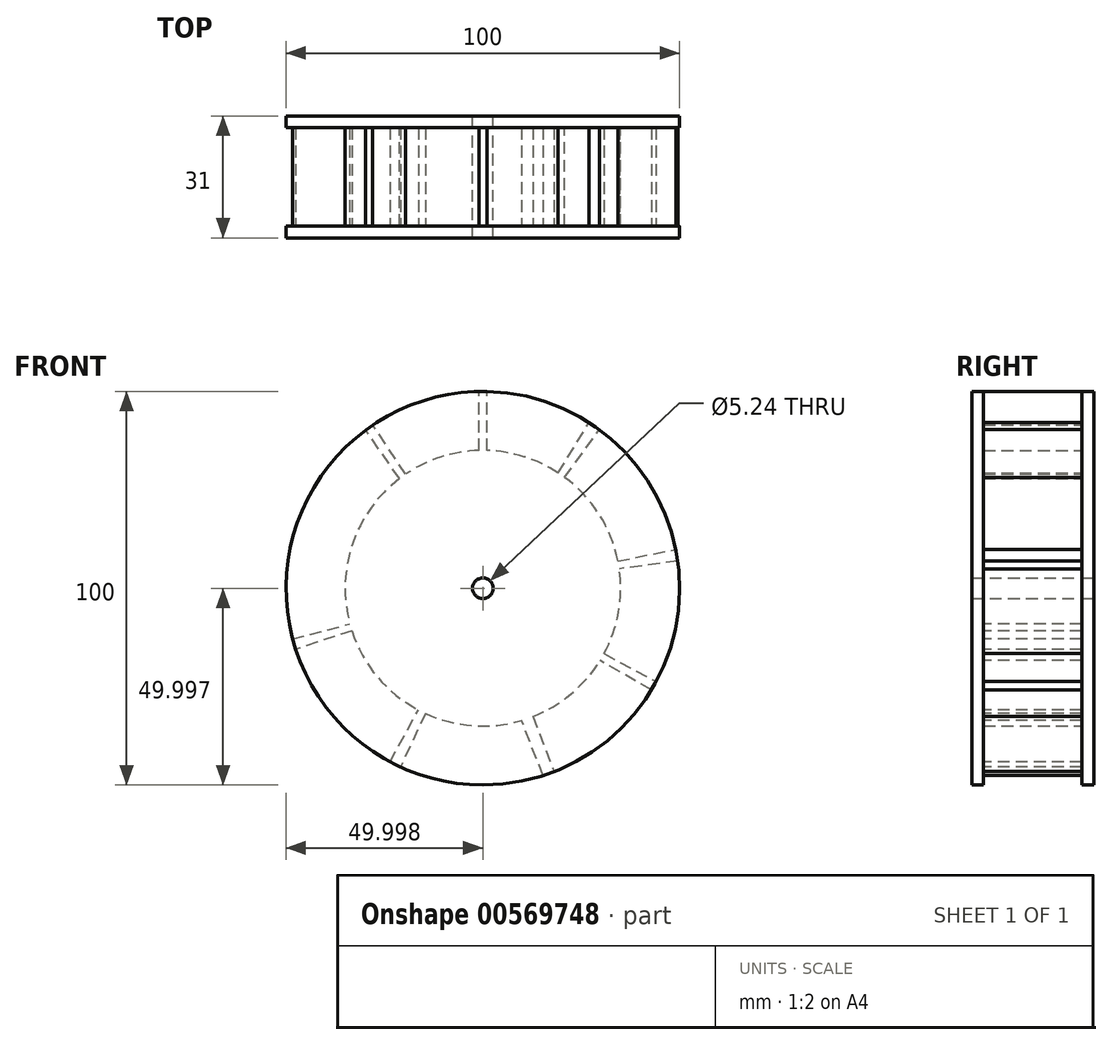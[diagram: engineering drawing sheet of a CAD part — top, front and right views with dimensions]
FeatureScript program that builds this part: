
annotation { "Feature Type Name" : "Feature", "Feature Type Description" : "" }
export const myFeature = defineFeature(function(context is Context, id is Id, definition is map)
    precondition{}
    {
        {
            var Q0;
            Q0=qCreatedBy(makeId("Front.planeOp"),FACE);
            var sketch = newSketch(context, id + "F0", { "sketchPlane" : qUnion([Q0])});
            skCircle(sketch, "E0", {"center": v(-6.77, 6) * mm, "radius": 50 * mm});
            skSolve(sketch);
        }
        {
            var Q0;
            Q0=makeQuery(id+"F0.imprint","IMPRINT",FACE,{"disambiguationData":[TD([[makeQuery(id+"F0.imprint","IMPRINT",EDGE,{"derivedFrom":sQuery(id+"F0.wireOp",EDGE,"E0")}),1.0]])]});
            extrude(context, id + "F1", {"entities" : qUnion([Q0]), "depth" : 3 * mm, "offsetDistance" : 25 * mm});
        }
        {
            var Q0;
            Q0=makeQuery(id+"F1.opExtrude","CAP_FACE",FACE,{"disambiguationData":[OSD([sQuery(id+"F0.wireOp",EDGE,"E0")])],"isStart":false});
            var sketch = newSketch(context, id + "F2", { "sketchPlane" : qUnion([Q0])});
            skCircle(sketch, "E1", {"center": v(-6.77, 6) * mm, "radius": 35 * mm});
            skSolve(sketch);
        }
        {
            var Q0;
            Q0=makeQuery(id+"F2.imprint","IMPRINT",FACE,{"disambiguationData":[TD([[makeQuery(id+"F2.imprint","IMPRINT",EDGE,{"derivedFrom":sQuery(id+"F2.wireOp",EDGE,"E1")}),1.0]])]});
            extrude(context, id + "F3", {"entities" : qUnion([Q0]), "operationType" : NewBodyOperationType.ADD, "depth" : 25 * mm, "offsetDistance" : 25 * mm});
        }
        {
            var Q0;
            Q0=makeQuery(id+"F3.opExtrude","CAP_FACE",FACE,{"disambiguationData":[OSD([sQuery(id+"F2.wireOp",EDGE,"E1")])],"isStart":false});
            var sketch = newSketch(context, id + "F4", { "sketchPlane" : qUnion([Q0])});
            skCircle(sketch, "E2", {"center": v(-6.77, 6) * mm, "radius": 50 * mm});
            skSolve(sketch);
        }
        {
            var Q0;
            Q0=makeQuery(id+"F4.imprint","IMPRINT",FACE,{"disambiguationData":[TD([[makeQuery(id+"F4.imprint","IMPRINT",EDGE,{"derivedFrom":makeQuery(id+"F3.opExtrude","CAP_EDGE",EDGE,{"disambiguationData":[OSD([sQuery(id+"F2.wireOp",EDGE,"E1")])],"isStart":false})}),1.0]])]});
            var Q1;
            Q1=makeQuery(id+"F4.imprint","IMPRINT",FACE,{"disambiguationData":[TD([[makeQuery(id+"F4.imprint","IMPRINT",EDGE,{"derivedFrom":sQuery(id+"F4.wireOp",EDGE,"E2")}),1.0]])]});
            extrude(context, id + "F5", {"entities" : qUnion([Q0, Q1]), "operationType" : NewBodyOperationType.ADD, "depth" : 3 * mm, "offsetDistance" : 25 * mm});
        }
        {
            var Q0;
            Q0=makeQuery(id+"F1.opExtrude","CAP_FACE",FACE,{"disambiguationData":[OSD([sQuery(id+"F0.wireOp",EDGE,"E0")])],"isStart":false});
            var sketch = newSketch(context, id + "F6", { "sketchPlane" : qUnion([Q0])});
            skLineSegment(sketch, "E3.bottom", {"start": v(-7.68, 41) * mm, "end": v(-5.68, 41) * mm});
            skLineSegment(sketch, "E3.top", {"start": v(-7.68, 56) * mm, "end": v(-5.68, 56) * mm});
            skLineSegment(sketch, "E3.left", {"start": v(-7.68, 41) * mm, "end": v(-7.68, 56) * mm});
            skLineSegment(sketch, "E3.right", {"start": v(-5.68, 41) * mm, "end": v(-5.68, 56) * mm});
            skLineSegment(sketch, "E4", {"start": v(-26.36, 35.01) * mm, "end": v(-34.75, 47.44) * mm});
            skLineSegment(sketch, "E5", {"start": v(-34.75, 47.44) * mm, "end": v(-36.53, 46.19) * mm});
            skLineSegment(sketch, "E6", {"start": v(-36.53, 46.19) * mm, "end": v(-27.98, 33.85) * mm});
            skLineSegment(sketch, "E7", {"start": v(-27.98, 33.85) * mm, "end": v(-26.36, 35.01) * mm});
            skLineSegment(sketch, "E8", {"start": v(12.34, 35.33) * mm, "end": v(20.24, 48.09) * mm});
            skLineSegment(sketch, "E9", {"start": v(20.24, 48.09) * mm, "end": v(22.87, 46.27) * mm});
            skLineSegment(sketch, "E10", {"start": v(22.87, 46.27) * mm, "end": v(13.98, 34.2) * mm});
            skLineSegment(sketch, "E11", {"start": v(12.34, 35.33) * mm, "end": v(13.98, 34.2) * mm});
            skSolve(sketch);
        }
        {
            var Q0;
            {var subQ0=sQuery(id+"F6.wireOp",EDGE,"E4");Q0=makeQuery(id+"F6.imprint","IMPRINT",FACE,{"disambiguationData":[TD([[makeQuery(id+"F6.imprint","IMPRINT",EDGE,{"derivedFrom":subQ0}),1.0]])]});}
            var Q1;
            Q1=makeQuery(id+"F6.imprint","IMPRINT",FACE,{"disambiguationData":[TD([[makeQuery(id+"F6.imprint","IMPRINT",EDGE,{"derivedFrom":sQuery(id+"F6.wireOp",EDGE,"E3.top")}),-1.0]])]});
            var Q2;
            {var subQ0=sQuery(id+"F6.wireOp",EDGE,"E8");Q2=makeQuery(id+"F6.imprint","IMPRINT",FACE,{"disambiguationData":[TD([[makeQuery(id+"F6.imprint","IMPRINT",EDGE,{"derivedFrom":subQ0}),-1.0]])]});}
            extrude(context, id + "F7", {"entities" : qUnion([Q0, Q1, Q2]), "operationType" : NewBodyOperationType.ADD, "depth" : 28 * mm, "offsetDistance" : 25 * mm});
        }
        {
            var Q0;
            {var subQ0=sQuery(id+"F4.wireOp",EDGE,"E2");var subQ1=makeQuery(id+"F5.opExtrude","CAP_FACE",FACE,{"disambiguationData":[OSD([subQ0])],"isStart":true});Q0=makeQuery(id+"F7.boolean.opBoolean","SPLIT",FACE,{"disambiguationData":[TD([makeQuery(id+"F3.opExtrude","SWEPT_FACE",FACE,{"disambiguationData":[OSD([sQuery(id+"F2.wireOp",EDGE,"E1")])]}),makeQuery(id+"F5.opExtrude","SWEPT_FACE",FACE,{"disambiguationData":[OSD([subQ0])]}),subQ1,makeQuery(id+"F7.opExtrude","SWEPT_FACE",FACE,{"disambiguationData":[OSD([sQuery(id+"F6.wireOp",EDGE,"E5")])]}),makeQuery(id+"F7.opExtrude","SWEPT_FACE",FACE,{"disambiguationData":[OSD([sQuery(id+"F6.wireOp",EDGE,"E6")])]}),makeQuery(id+"F7.opExtrude","SWEPT_FACE",FACE,{"disambiguationData":[OSD([sQuery(id+"F6.wireOp",EDGE,"E9")])]}),makeQuery(id+"F7.opExtrude","SWEPT_FACE",FACE,{"disambiguationData":[OSD([sQuery(id+"F6.wireOp",EDGE,"E10")])]})])],"derivedFrom":subQ1});}
            var sketch = newSketch(context, id + "F8", { "sketchPlane" : qUnion([Q0])});
            skLineSegment(sketch, "E12", {"start": v(-27.54, 12.9) * mm, "end": v(-42.25, 15.87) * mm});
            skLineSegment(sketch, "E13", {"start": v(-42.25, 15.87) * mm, "end": v(-42.75, 12.9) * mm});
            skLineSegment(sketch, "E14", {"start": v(-42.75, 12.9) * mm, "end": v(-27.88, 10.94) * mm});
            skLineSegment(sketch, "E15", {"start": v(-27.88, 10.94) * mm, "end": v(-27.54, 12.9) * mm});
            skLineSegment(sketch, "E16", {"start": v(-24.03, -10.6) * mm, "end": v(-37.24, -17.72) * mm});
            skLineSegment(sketch, "E17", {"start": v(-37.24, -17.72) * mm, "end": v(-36.05, -19.8) * mm});
            skLineSegment(sketch, "E18", {"start": v(-36.05, -19.8) * mm, "end": v(-23.01, -12.37) * mm});
            skLineSegment(sketch, "E19", {"start": v(-23.01, -12.37) * mm, "end": v(-24.03, -10.6) * mm});
            skLineSegment(sketch, "E20", {"start": v(-5.92, -26.61) * mm, "end": v(-11.36, -40.6) * mm});
            skLineSegment(sketch, "E21", {"start": v(-11.36, -40.6) * mm, "end": v(-8.53, -41.6) * mm});
            skLineSegment(sketch, "E22", {"start": v(-8.53, -41.6) * mm, "end": v(-3.08, -27.58) * mm});
            skLineSegment(sketch, "E23", {"start": v(-3.08, -27.58) * mm, "end": v(-5.92, -26.61) * mm});
            skSolve(sketch);
        }
        {
            var Q0;
            {var subQ0=sQuery(id+"F8.wireOp",EDGE,"E12");Q0=makeQuery(id+"F8.imprint","IMPRINT",FACE,{"disambiguationData":[TD([[makeQuery(id+"F8.imprint","IMPRINT",EDGE,{"derivedFrom":subQ0}),1.0]])]});}
            var Q1;
            {var subQ0=sQuery(id+"F8.wireOp",EDGE,"E16");Q1=makeQuery(id+"F8.imprint","IMPRINT",FACE,{"disambiguationData":[TD([[makeQuery(id+"F8.imprint","IMPRINT",EDGE,{"derivedFrom":subQ0}),1.0]])]});}
            var Q2;
            {var subQ0=sQuery(id+"F8.wireOp",EDGE,"E20");Q2=makeQuery(id+"F8.imprint","IMPRINT",FACE,{"disambiguationData":[TD([[makeQuery(id+"F8.imprint","IMPRINT",EDGE,{"derivedFrom":subQ0}),1.0]])]});}
            extrude(context, id + "F9", {"entities" : qUnion([Q0, Q1, Q2]), "operationType" : NewBodyOperationType.ADD, "depth" : 28 * mm, "offsetDistance" : 25 * mm});
        }
        {
            var Q0;
            {var subQ0=makeQuery(id+"F7.opExtrude","SWEPT_FACE",FACE,{"disambiguationData":[OSD([sQuery(id+"F6.wireOp",EDGE,"E5")])]});var subQ1=sQuery(id+"F4.wireOp",EDGE,"E2");var subQ2=makeQuery(id+"F5.opExtrude","SWEPT_FACE",FACE,{"disambiguationData":[OSD([subQ1])]});var subQ3=makeQuery(id+"F5.opExtrude","CAP_FACE",FACE,{"disambiguationData":[OSD([subQ1])],"isStart":true});var subQ4=makeQuery(id+"F3.opExtrude","SWEPT_FACE",FACE,{"disambiguationData":[OSD([sQuery(id+"F2.wireOp",EDGE,"E1")])]});var subQ5=makeQuery(id+"F7.opExtrude","SWEPT_FACE",FACE,{"disambiguationData":[OSD([sQuery(id+"F6.wireOp",EDGE,"E6")])]});Q0=makeQuery(id+"F9.boolean.opBoolean","SPLIT",FACE,{"disambiguationData":[TD([subQ4,subQ2,subQ3,subQ0,subQ5,makeQuery(id+"F9.opExtrude","SWEPT_FACE",FACE,{"disambiguationData":[OSD([sQuery(id+"F8.wireOp",EDGE,"E21")])]}),makeQuery(id+"F9.opExtrude","SWEPT_FACE",FACE,{"disambiguationData":[OSD([sQuery(id+"F8.wireOp",EDGE,"E22")])]})])],"derivedFrom":makeQuery(id+"F7.boolean.opBoolean","SPLIT",FACE,{"disambiguationData":[TD([subQ4,subQ2,subQ3,subQ0,subQ5,makeQuery(id+"F7.opExtrude","SWEPT_FACE",FACE,{"disambiguationData":[OSD([sQuery(id+"F6.wireOp",EDGE,"E9")])]}),makeQuery(id+"F7.opExtrude","SWEPT_FACE",FACE,{"disambiguationData":[OSD([sQuery(id+"F6.wireOp",EDGE,"E10")])]})])],"derivedFrom":subQ3})});}
            var sketch = newSketch(context, id + "F10", { "sketchPlane" : qUnion([Q0])});
            skLineSegment(sketch, "E24", {"start": v(21.38, -25.8) * mm, "end": v(27.64, -39.43) * mm});
            skLineSegment(sketch, "E25", {"start": v(30.33, -38.1) * mm, "end": v(23.18, -24.91) * mm});
            skLineSegment(sketch, "E26", {"start": v(23.18, -24.91) * mm, "end": v(21.38, -25.8) * mm});
            skLineSegment(sketch, "E27", {"start": v(30.33, -38.1) * mm, "end": v(27.64, -39.43) * mm});
            skLineSegment(sketch, "E28", {"start": v(40.05, -4.84) * mm, "end": v(54.3, -9.49) * mm});
            skLineSegment(sketch, "E29", {"start": v(54.3, -9.49) * mm, "end": v(55.07, -6.94) * mm});
            skLineSegment(sketch, "E30", {"start": v(55.07, -6.94) * mm, "end": v(40.58, -3.06) * mm});
            skLineSegment(sketch, "E31", {"start": v(40.58, -3.06) * mm, "end": v(40.05, -4.84) * mm});
            skSolve(sketch);
        }
        {
            var Q0;
            {var subQ0=sQuery(id+"F10.wireOp",EDGE,"E24");Q0=makeQuery(id+"F10.imprint","IMPRINT",FACE,{"disambiguationData":[TD([[makeQuery(id+"F10.imprint","IMPRINT",EDGE,{"derivedFrom":subQ0}),1.0]])]});}
            var Q1;
            {var subQ0=sQuery(id+"F10.wireOp",EDGE,"E28");Q1=makeQuery(id+"F10.imprint","IMPRINT",FACE,{"disambiguationData":[TD([[makeQuery(id+"F10.imprint","IMPRINT",EDGE,{"derivedFrom":subQ0}),1.0]])]});}
            extrude(context, id + "F11", {"entities" : qUnion([Q0, Q1]), "operationType" : NewBodyOperationType.ADD, "depth" : 28 * mm, "offsetDistance" : 25 * mm});
        }
        {
            var Q0;
            Q0=makeQuery(id+"F1.opExtrude","CAP_FACE",FACE,{"disambiguationData":[OSD([sQuery(id+"F0.wireOp",EDGE,"E0")])],"isStart":true});
            var sketch = newSketch(context, id + "F12", { "sketchPlane" : qUnion([Q0])});
            skCircle(sketch, "E32", {"center": v(6.77, 6) * mm, "radius": 2.62 * mm});
            skSolve(sketch);
        }
        {
            var Q0;
            Q0=makeQuery(id+"F12.imprint","IMPRINT",FACE,{"disambiguationData":[TD([[makeQuery(id+"F12.imprint","IMPRINT",EDGE,{"derivedFrom":sQuery(id+"F12.wireOp",EDGE,"E32")}),1.0]])]});
            extrude(context, id + "F13", {"entities" : qUnion([Q0]), "operationType" : NewBodyOperationType.REMOVE, "endBound" : BoundingType.THROUGH_ALL, "oppositeDirection" : true, "depth" : 25 * mm, "offsetDistance" : 25 * mm});
        }
    });
